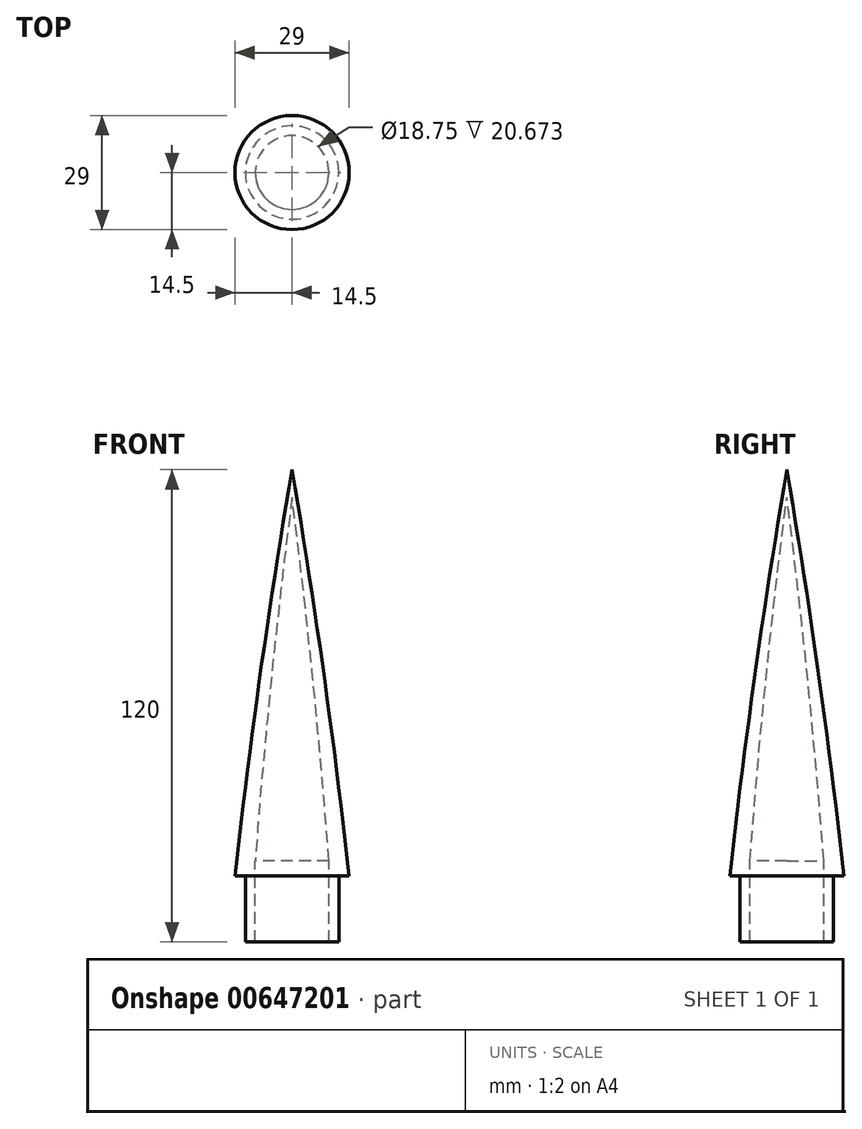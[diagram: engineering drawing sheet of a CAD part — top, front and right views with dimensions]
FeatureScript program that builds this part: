
annotation { "Feature Type Name" : "Feature", "Feature Type Description" : "" }
export const myFeature = defineFeature(function(context is Context, id is Id, definition is map)
    precondition{}
    {
        {
            var Q0;
            Q0=qCreatedBy(makeId("Front.planeOp"),FACE);
            var sketch = newSketch(context, id + "F0", { "sketchPlane" : qUnion([Q0])});
            skLineSegment(sketch, "E0", {"start": v(-11.87, 0) * mm, "end": v(-11.87, 16.75) * mm});
            skLineSegment(sketch, "E1", {"start": v(-11.88, 16.75) * mm, "end": v(-14.5, 16.75) * mm});
            skPoint(sketch, "E2", {"position": v(0, 120) * mm});
            skPoint(sketch, "E3", {"position": v(-11.88, 16.75) * mm});
            skArc(sketch, "E4", {"start": v(0, 120) * mm, "mid": v(-8.01, 68.48) * mm, "end": v(-14.5, 16.75) * mm});
            skLineSegment(sketch, "E5", {"start": v(-11.87, 0) * mm, "end": v(-9.37, 0) * mm});
            skPoint(sketch, "E6", {"position": v(0, 113) * mm});
            skLineSegment(sketch, "E7", {"start": v(-9.37, 20.67) * mm, "end": v(-9.37, 0) * mm});
            skArc(sketch, "E8", {"start": v(0, 113) * mm, "mid": v(-5.28, 66.9) * mm, "end": v(-9.37, 20.67) * mm});
            skLineSegment(sketch, "E9", {"start": v(0, 120) * mm, "end": v(0, 113) * mm});
            skPoint(sketch, "E10", {"position": v(-9, 61.3) * mm});
            skPoint(sketch, "E11", {"position": v(-41.3, 113.14) * mm});
            skSolve(sketch);
        }
        {
            var Q0;
            Q0=qCreatedBy(makeId("Front.planeOp"),FACE);
            var sketch = newSketch(context, id + "F1", { "sketchPlane" : qUnion([Q0])});
            skLineSegment(sketch, "E12", {"start": v(0, 14.17) * mm, "end": v(0, -34.8) * mm});
            skSolve(sketch);
        }
        {
            var Q0;
            Q0=makeQuery(id+"F0.imprint","IMPRINT",FACE,{"disambiguationData":[TD([[makeQuery(id+"F0.imprint","IMPRINT",EDGE,{"derivedFrom":sQuery(id+"F0.wireOp",EDGE,"E0")}),-1.0]])]});
            var Q1;
            Q1=sQuery(id+"F1.wireOp",EDGE,"E12");
            revolve(context, id + "F2", {"entities" : qUnion([Q0]), "axis" : qUnion([Q1]), "revolveType" : RevolveType.FULL});
        }
    });
